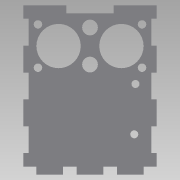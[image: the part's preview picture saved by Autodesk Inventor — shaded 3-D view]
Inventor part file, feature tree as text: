
AUTODESK INVENTOR PART (.ipt)
format: ipt  version: 2015 SP1 (Build 190203100, 203)  size: 218,624 bytes
history: native  units: mm
features: extrude x3, sketch x3
ambient origin geometry x8: Origin, YZ Plane, XZ Plane, XY Plane, X Axis, Y Axis, Z Axis, Center Point
bodies: Body1 (feature_tree)
feature tree (6):
  extrude  "Extrusion2"  Depth=3.0mm
  extrude  "Extrusion3"  Depth=3.0mm
  extrude  "Extrusion4"  Depth=3.0mm
  sketch  "Sketch1"  dims[d0=10.0mm d1=3.0mm]
  sketch  "Sketch2"  dims[d2=20.0mm d4=15.0mm d5=20.0mm d7=15.0mm d13=3.0mm]
  sketch  "Sketch3"  dims[d14=180.0deg d15=3.0mm d17=7.675mm d18=7.675mm d21=3.0mm d22=0.0mm d23=2.999814mm d24=1.0mm d25=1.0mm d26=3.0mm d27=0.0mm d28=1.0mm d29=1.0mm d30=11.700171mm d31=11.699829mm d32=7.675mm d33=7.675mm d34=11.699829mm d35=11.700171mm d45=8.061mm d46=8.061mm d47=2.0mm d48=2.0mm d49=3.0mm d50=0.0mm]
